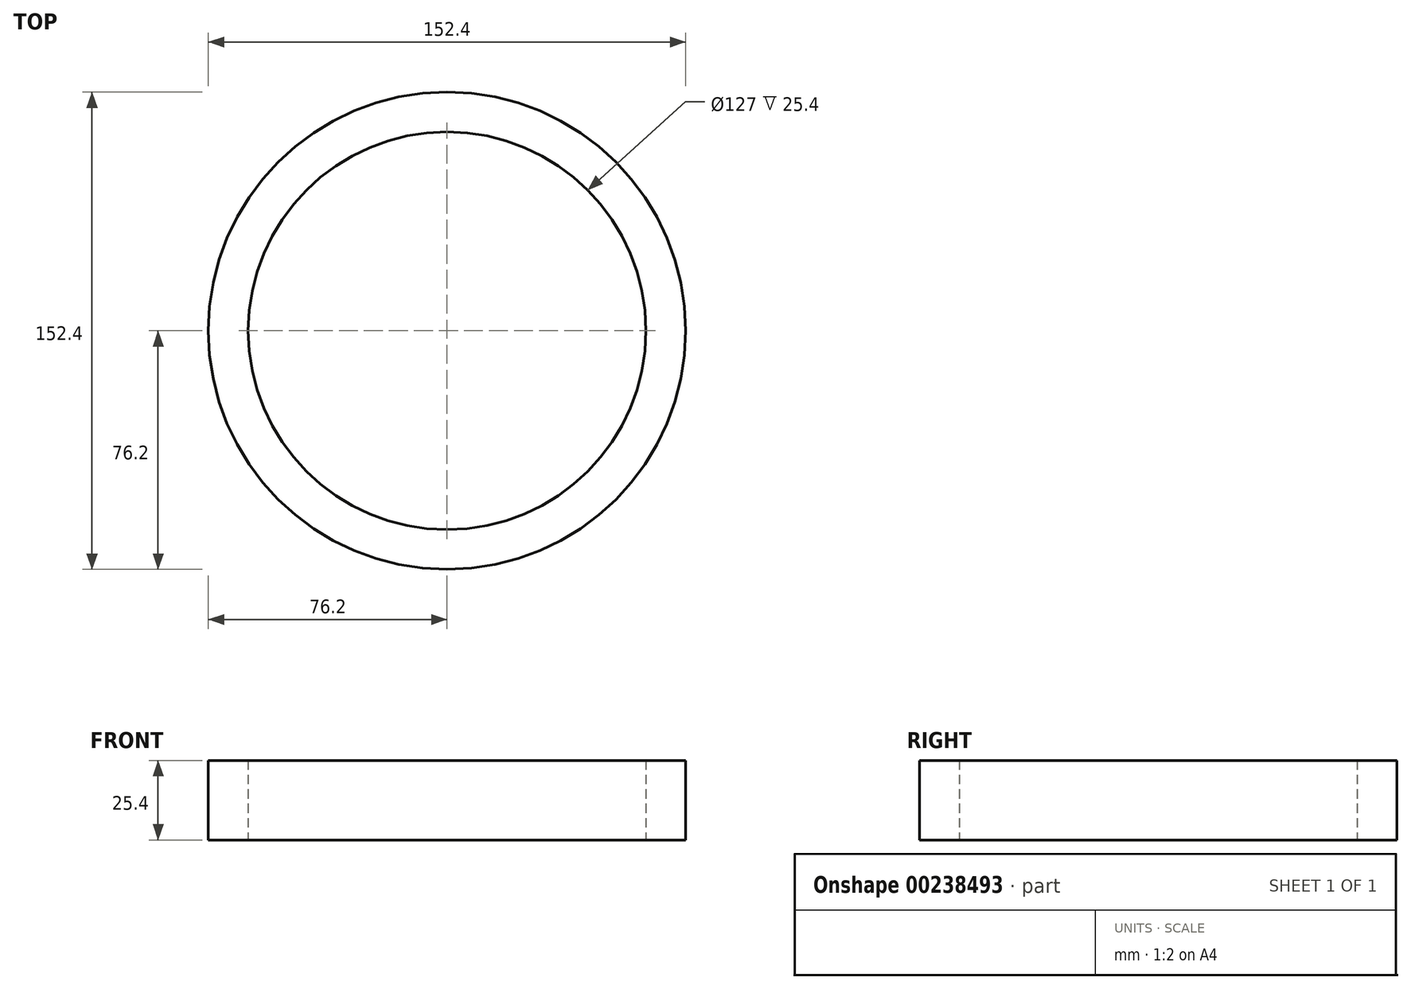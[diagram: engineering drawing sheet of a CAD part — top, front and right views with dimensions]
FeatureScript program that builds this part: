
annotation { "Feature Type Name" : "Feature", "Feature Type Description" : "" }
export const myFeature = defineFeature(function(context is Context, id is Id, definition is map)
    precondition{}
    {
        {
            var Q0;
            Q0=qCreatedBy(makeId("Top.planeOp"),FACE);
            var sketch = newSketch(context, id + "F0", { "sketchPlane" : qUnion([Q0])});
            skCircle(sketch, "E0", {"center": v(0, 0) * mm, "radius": 76.2 * mm});
            skCircle(sketch, "E1", {"center": v(0, 0) * mm, "radius": 12.7 * mm});
            skLineSegment(sketch, "E2", {"start": v(0, 0) * mm, "end": v(0, 76.2) * mm});
            skLineSegment(sketch, "E3.0", {"start": v(12.7, 0) * mm, "end": v(12.7, 76.2) * mm});
            skLineSegment(sketch, "E4.0", {"start": v(-12.7, 0) * mm, "end": v(-12.7, 76.2) * mm});
            skLineSegment(sketch, "E5", {"start": v(0, 0) * mm, "end": v(0, -76.2) * mm});
            skLineSegment(sketch, "E6.0", {"start": v(-12.7, 0) * mm, "end": v(-12.7, -76.2) * mm});
            skLineSegment(sketch, "E7.0", {"start": v(12.7, 0) * mm, "end": v(12.7, -76.2) * mm});
            skLineSegment(sketch, "E8", {"start": v(0, 0) * mm, "end": v(-76.2, 0) * mm});
            skLineSegment(sketch, "E9.0", {"start": v(0, -12.7) * mm, "end": v(-76.2, -12.7) * mm});
            skLineSegment(sketch, "E10.0", {"start": v(0, 12.7) * mm, "end": v(-76.2, 12.7) * mm});
            skLineSegment(sketch, "E11", {"start": v(0, 0) * mm, "end": v(76.2, 0) * mm});
            skLineSegment(sketch, "E12.0", {"start": v(0, 12.7) * mm, "end": v(76.2, 12.7) * mm});
            skLineSegment(sketch, "E13.0", {"start": v(0, -12.7) * mm, "end": v(76.2, -12.7) * mm});
            skCircle(sketch, "E14", {"center": v(0, 0) * mm, "radius": 63.5 * mm});
            skSolve(sketch);
        }
        {
            var Q0;
            Q0 = qSketchRegion(id + "F0", true);
            extrude(context, id + "F1", {"entities" : qUnion([Q0]), "depth" : 25.4 * mm});
        }
    });
